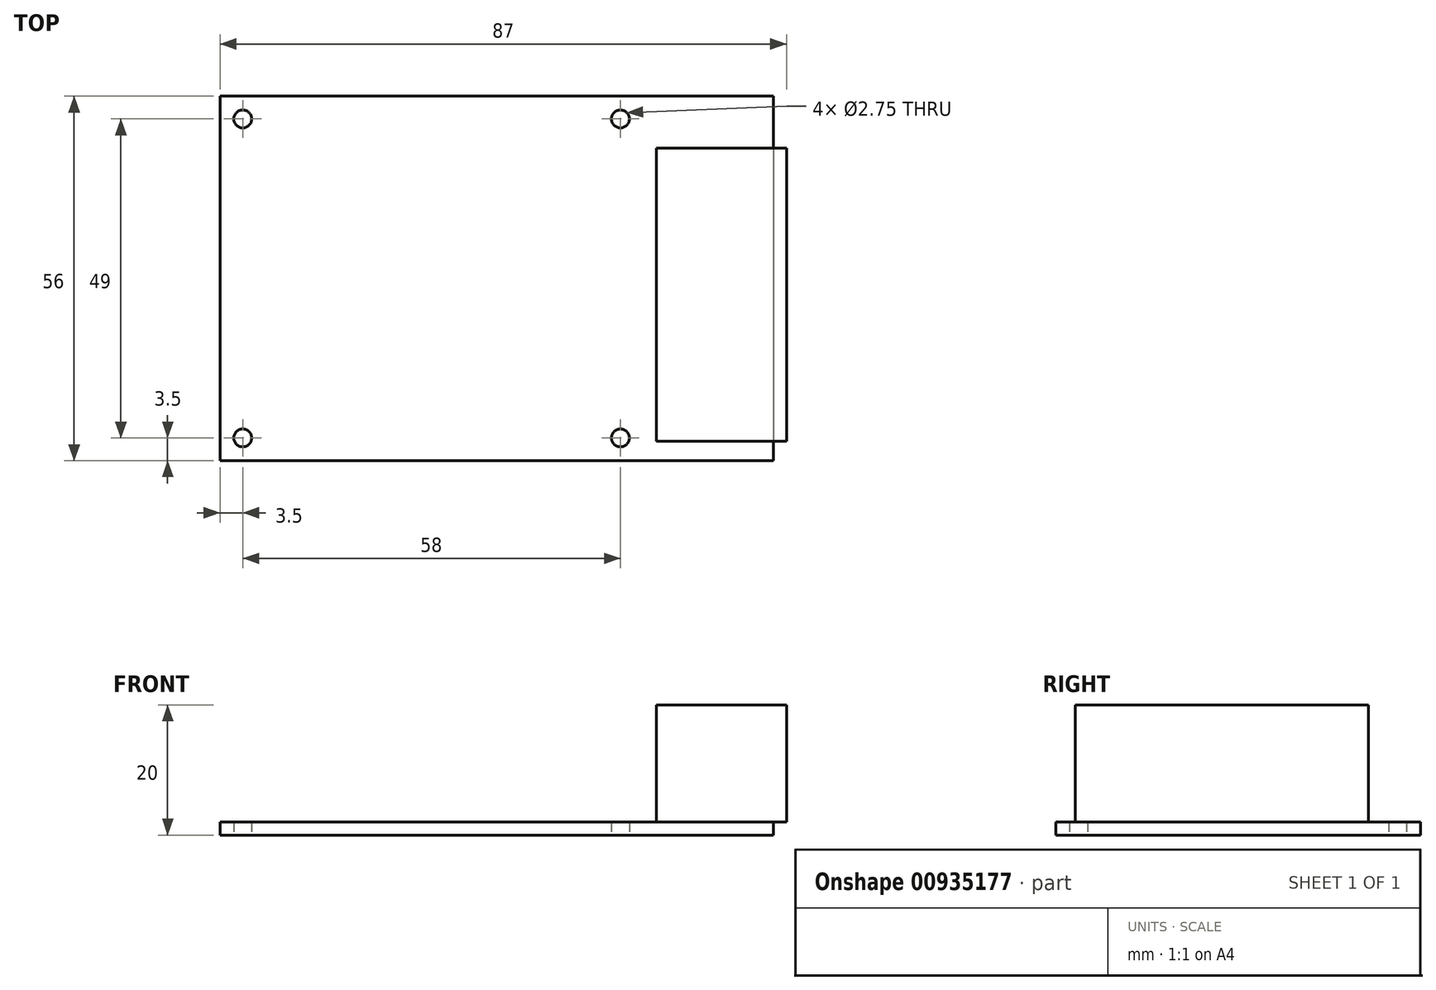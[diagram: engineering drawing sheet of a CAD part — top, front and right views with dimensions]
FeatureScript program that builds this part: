
annotation { "Feature Type Name" : "Feature", "Feature Type Description" : "" }
export const myFeature = defineFeature(function(context is Context, id is Id, definition is map)
    precondition{}
    {
        {
            var Q0;
            Q0=qCreatedBy(makeId("Top.planeOp"),FACE);
            var sketch = newSketch(context, id + "F0", { "sketchPlane" : qUnion([Q0])});
            skLineSegment(sketch, "E0.bottom", {"start": v(42.5, 28) * mm, "end": v(-42.5, 28) * mm});
            skLineSegment(sketch, "E0.top", {"start": v(42.5, -28) * mm, "end": v(-42.5, -28) * mm});
            skLineSegment(sketch, "E0.left", {"start": v(42.5, 28) * mm, "end": v(42.5, -28) * mm});
            skLineSegment(sketch, "E0.right", {"start": v(-42.5, 28) * mm, "end": v(-42.5, -28) * mm});
            skPoint(sketch, "E0.middle", {"position": v(0, 0) * mm});
            skLineSegment(sketch, "E1.bottom", {"start": v(-39, 24.5) * mm, "end": v(19, 24.5) * mm, "construction": true});
            skLineSegment(sketch, "E1.top", {"start": v(-39, -24.5) * mm, "end": v(19, -24.5) * mm, "construction": true});
            skLineSegment(sketch, "E1.left", {"start": v(-39, 24.5) * mm, "end": v(-39, -24.5) * mm, "construction": true});
            skLineSegment(sketch, "E1.right", {"start": v(19, 24.5) * mm, "end": v(19, -24.5) * mm, "construction": true});
            skCircle(sketch, "E2", {"center": v(-39, 24.5) * mm, "radius": 1.38 * mm});
            skCircle(sketch, "E3", {"center": v(19, 24.5) * mm, "radius": 1.38 * mm});
            skCircle(sketch, "E4", {"center": v(19, -24.5) * mm, "radius": 1.38 * mm});
            skCircle(sketch, "E5", {"center": v(-39, -24.5) * mm, "radius": 1.38 * mm});
            skSolve(sketch);
        }
        {
            var Q0;
            Q0=makeQuery(id+"F0.imprint","IMPRINT",FACE,{"disambiguationData":[TD([[makeQuery(id+"F0.imprint","IMPRINT",EDGE,{"derivedFrom":sQuery(id+"F0.wireOp",EDGE,"E0.bottom")}),1.0]])]});
            extrude(context, id + "F1", {"entities" : qUnion([Q0]), "depth" : 2 * mm, "offsetDistance" : 25 * mm});
        }
        {
            var Q0;
            Q0=makeQuery(id+"F1.opExtrude","CAP_FACE",FACE,{"disambiguationData":[OSD([sQuery(id+"F0.wireOp",EDGE,"E0.bottom"),sQuery(id+"F0.wireOp",EDGE,"E0.top"),sQuery(id+"F0.wireOp",EDGE,"E0.left"),sQuery(id+"F0.wireOp",EDGE,"E0.right"),sQuery(id+"F0.wireOp",EDGE,"E2"),sQuery(id+"F0.wireOp",EDGE,"E3"),sQuery(id+"F0.wireOp",EDGE,"E4"),sQuery(id+"F0.wireOp",EDGE,"E5")])],"isStart":false});
            var sketch = newSketch(context, id + "F2", { "sketchPlane" : qUnion([Q0])});
            skLineSegment(sketch, "E6.bottom", {"start": v(24.5, 20) * mm, "end": v(44.5, 20) * mm});
            skLineSegment(sketch, "E6.top", {"start": v(24.5, -25) * mm, "end": v(44.5, -25) * mm});
            skLineSegment(sketch, "E6.left", {"start": v(24.5, 20) * mm, "end": v(24.5, -25) * mm});
            skLineSegment(sketch, "E6.right", {"start": v(44.5, 20) * mm, "end": v(44.5, -25) * mm});
            skSolve(sketch);
        }
        {
            var Q0;
            Q0=qSketchRegion(id+"F2",true);
            extrude(context, id + "F3", {"entities" : qUnion([Q0]), "depth" : 18 * mm, "offsetDistance" : 25 * mm});
        }
    });
